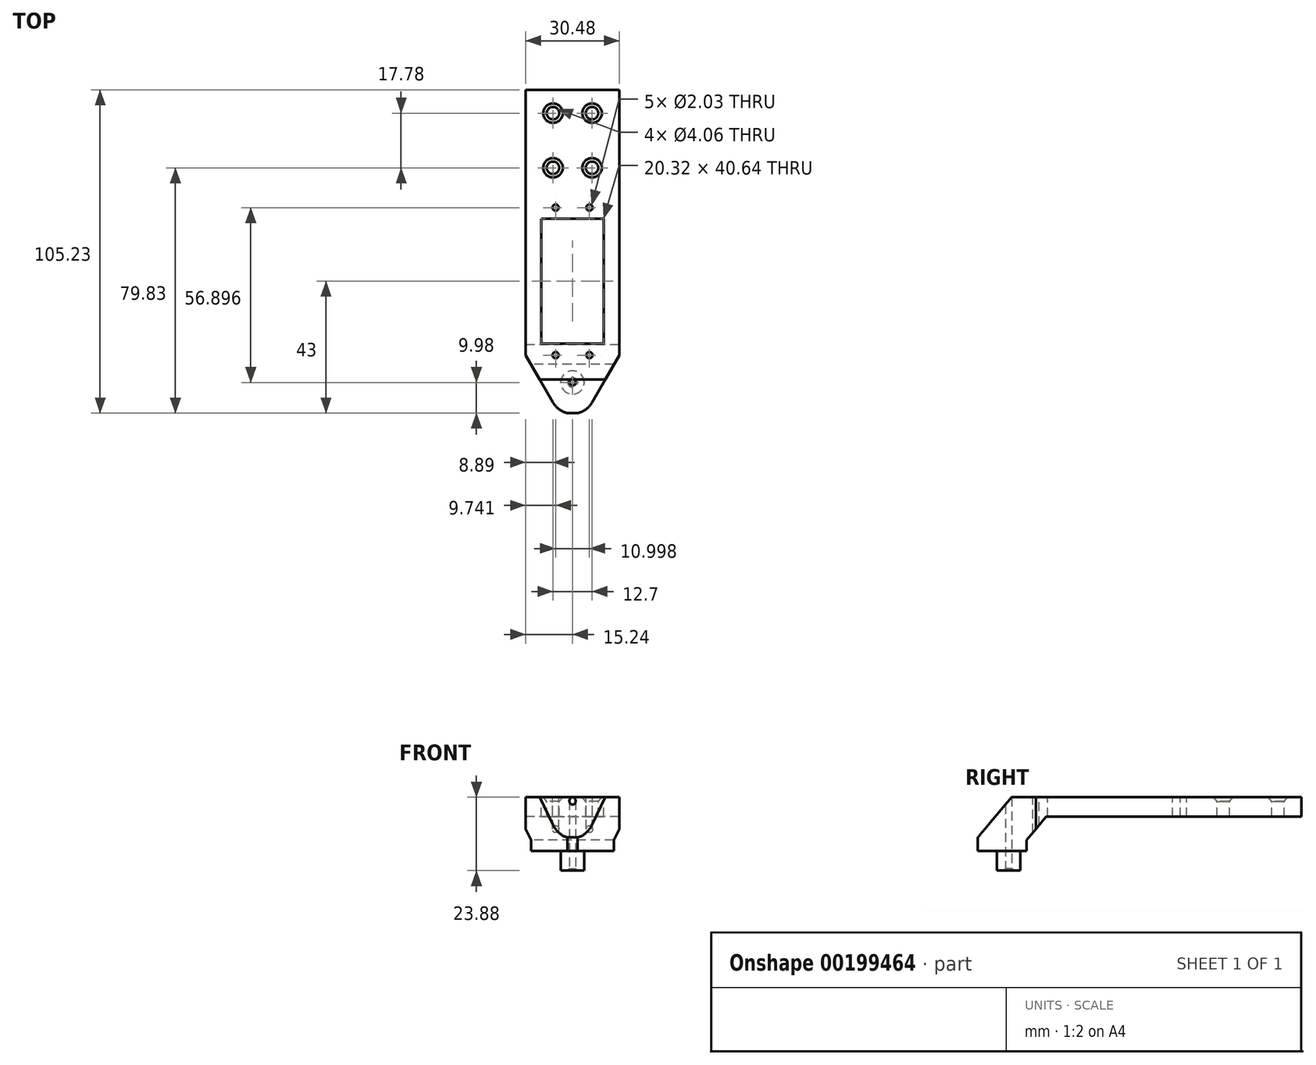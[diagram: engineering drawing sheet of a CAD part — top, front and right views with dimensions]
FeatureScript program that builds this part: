
annotation { "Feature Type Name" : "Feature", "Feature Type Description" : "" }
export const myFeature = defineFeature(function(context is Context, id is Id, definition is map)
    precondition{}
    {
        {
            var Q0;
            Q0=qCreatedBy(makeId("Top.planeOp"),FACE);
            var sketch = newSketch(context, id + "F0", { "sketchPlane" : qUnion([Q0])});
            skCircle(sketch, "E0", {"center": v(0, 0) * mm, "radius": 6.35 * mm});
            skLineSegment(sketch, "E1", {"start": v(-10.16, -10.16) * mm, "end": v(10.16, -10.16) * mm});
            skLineSegment(sketch, "E2", {"start": v(10.16, -10.16) * mm, "end": v(10.16, 30.48) * mm});
            skLineSegment(sketch, "E3", {"start": v(10.16, 30.48) * mm, "end": v(-10.16, 30.48) * mm});
            skLineSegment(sketch, "E4", {"start": v(-10.16, 30.48) * mm, "end": v(-10.16, -10.16) * mm});
            skLineSegment(sketch, "E5", {"start": v(15.24, -13.97) * mm, "end": v(-15.24, -13.97) * mm});
            skLineSegment(sketch, "E6", {"start": v(-15.24, -13.97) * mm, "end": v(-15.24, 40.64) * mm});
            skLineSegment(sketch, "E7", {"start": v(-15.24, 40.64) * mm, "end": v(15.24, 40.64) * mm});
            skLineSegment(sketch, "E8", {"start": v(15.24, 40.64) * mm, "end": v(15.24, -13.97) * mm});
            skPoint(sketch, "E9", {"position": v(-5.5, 34.04) * mm});
            skPoint(sketch, "E10", {"position": v(5.5, 34.04) * mm});
            skCircle(sketch, "E11", {"center": v(0, -22.86) * mm, "radius": 3.81 * mm, "construction": true});
            skCircle(sketch, "E12", {"center": v(-5.5, 34.04) * mm, "radius": 1.02 * mm});
            skCircle(sketch, "E13", {"center": v(5.5, 34.04) * mm, "radius": 1.02 * mm});
            skCircle(sketch, "E14", {"center": v(-5.5, -13.97) * mm, "radius": 1.02 * mm});
            skCircle(sketch, "E15", {"center": v(5.5, -13.97) * mm, "radius": 1.02 * mm});
            skLineSegment(sketch, "E16", {"start": v(15.24, -13.97) * mm, "end": v(6.35, -29.37) * mm});
            skLineSegment(sketch, "E17", {"start": v(-15.24, -13.97) * mm, "end": v(-6.35, -29.37) * mm});
            skArc(sketch, "E18", {"start": v(-6.35, -29.37) * mm, "mid": v(0, -33.03) * mm, "end": v(6.35, -29.37) * mm});
            skLineSegment(sketch, "E19", {"start": v(-15.24, 40.64) * mm, "end": v(-15.24, 72.4) * mm});
            skLineSegment(sketch, "E20", {"start": v(-15.24, 72.4) * mm, "end": v(15.24, 72.4) * mm});
            skLineSegment(sketch, "E21", {"start": v(15.24, 72.4) * mm, "end": v(15.24, 40.64) * mm});
            skPoint(sketch, "E22", {"position": v(0, 72.4) * mm});
            skLineSegment(sketch, "E23", {"start": v(0, 72.4) * mm, "end": v(0, 40.64) * mm});
            skPoint(sketch, "E24", {"position": v(6.35, 64.77) * mm});
            skPoint(sketch, "E25", {"position": v(6.35, 47) * mm});
            skPoint(sketch, "E26", {"position": v(-6.35, 64.77) * mm});
            skPoint(sketch, "E27", {"position": v(-6.35, 47) * mm});
            skSolve(sketch);
        }
        {
            var Q0;
            Q0=qCreatedBy(makeId("Right.planeOp"),FACE);
            var sketch = newSketch(context, id + "F1", { "sketchPlane" : qUnion([Q0])});
            skPoint(sketch, "E28", {"position": v(-21.85, 0) * mm});
            skPoint(sketch, "E29", {"position": v(40.64, 0) * mm});
            skLineSegment(sketch, "E30", {"start": v(40.64, 0) * mm, "end": v(-21.85, 0) * mm});
            skLineSegment(sketch, "E31", {"start": v(40.64, 0) * mm, "end": v(40.64, -6.35) * mm});
            skPoint(sketch, "E32", {"position": v(-10.16, 0) * mm});
            skPoint(sketch, "E33", {"position": v(-10.6, -6.35) * mm});
            skLineSegment(sketch, "E34", {"start": v(40.64, -6.35) * mm, "end": v(-10.6, -6.35) * mm});
            skLineSegment(sketch, "E35", {"start": v(-10.6, -6.35) * mm, "end": v(-16.99, -13.97) * mm});
            skLineSegment(sketch, "E36", {"start": v(-16.99, -17.53) * mm, "end": v(-32.84, -17.53) * mm});
            skLineSegment(sketch, "E37", {"start": v(-16.99, -13.97) * mm, "end": v(-16.99, -17.53) * mm});
            skLineSegment(sketch, "E38", {"start": v(-32.84, -17.53) * mm, "end": v(-32.84, -13.97) * mm});
            skLineSegment(sketch, "E39", {"start": v(-32.84, -13.97) * mm, "end": v(-32.84, -13.1) * mm});
            skLineSegment(sketch, "E40", {"start": v(-32.84, -13.1) * mm, "end": v(-21.85, 0) * mm});
            skLineSegment(sketch, "E41", {"start": v(40.64, 0) * mm, "end": v(83.81, 0) * mm});
            skLineSegment(sketch, "E42", {"start": v(83.81, 0) * mm, "end": v(83.81, -6.35) * mm});
            skLineSegment(sketch, "E43", {"start": v(83.81, -6.35) * mm, "end": v(40.64, -6.35) * mm});
            skSolve(sketch);
        }
        {
            var Q0;
            Q0 = qSketchRegion(id + "F0", true);
            var Q1;
            Q1=sQuery(id+"F1.wireOp",VERTEX,"E38.start");
            extrude(context, id + "F2", {"entities" : qUnion([Q0]), "endBound" : BoundingType.UP_TO_VERTEX, "oppositeDirection" : true, "endBoundEntityVertex" : qUnion([Q1]), "depth" : 25.4 * mm});
        }
        {
            var Q0;
            Q0 = qSketchRegion(id + "F1", true);
            extrude(context, id + "F3", {"entities" : qUnion([Q0]), "operationType" : NewBodyOperationType.INTERSECT, "endBound" : BoundingType.SYMMETRIC, "depth" : 254 * mm});
        }
        {
            var Q0;
            Q0=makeQuery(id+"F2.opExtrude","CAP_FACE",FACE,{"disambiguationData":[OSD([sQuery(id+"F0.wireOp",EDGE,"E1"),sQuery(id+"F0.wireOp",EDGE,"E2"),sQuery(id+"F0.wireOp",EDGE,"E3"),sQuery(id+"F0.wireOp",EDGE,"E4"),sQuery(id+"F0.wireOp",EDGE,"E6"),sQuery(id+"F0.wireOp",EDGE,"E8"),sQuery(id+"F0.wireOp",EDGE,"E12"),sQuery(id+"F0.wireOp",EDGE,"E13"),sQuery(id+"F0.wireOp",EDGE,"E14"),sQuery(id+"F0.wireOp",EDGE,"E15"),sQuery(id+"F0.wireOp",EDGE,"E16"),sQuery(id+"F0.wireOp",EDGE,"E17"),sQuery(id+"F0.wireOp",EDGE,"E18"),sQuery(id+"F0.wireOp",EDGE,"E19"),sQuery(id+"F0.wireOp",EDGE,"E20"),sQuery(id+"F0.wireOp",EDGE,"E21")])],"isStart":false});
            var sketch = newSketch(context, id + "F4", { "sketchPlane" : qUnion([Q0])});
            skPoint(sketch, "E44", {"position": v(0, 22.86) * mm});
            skCircle(sketch, "E45", {"center": v(0, 22.86) * mm, "radius": 3.81 * mm});
            skSolve(sketch);
        }
        {
            var Q0;
            Q0 = qSketchRegion(id + "F4", true);
            extrude(context, id + "F5", {"entities" : qUnion([Q0]), "operationType" : NewBodyOperationType.ADD, "depth" : 6.35 * mm});
        }
        {
            var Q0;
            Q0=makeQuery(id+"F5.opExtrude","CAP_FACE",FACE,{"disambiguationData":[OSD([sQuery(id+"F4.wireOp",EDGE,"E45")])],"isStart":false});
            var sketch = newSketch(context, id + "F6", { "sketchPlane" : qUnion([Q0])});
            skPoint(sketch, "E46", {"position": v(0, 22.86) * mm});
            skSolve(sketch);
        }
        {
            var Q0;
            Q0=sQuery(id+"F6.wireOp",VERTEX,"E46");
            var Q1;
            Q1=makeQuery(id+"F2.opExtrude","SWEPT_BODY",BODY,{"disambiguationData":[OSD([sQuery(id+"F0.wireOp",EDGE,"E1"),sQuery(id+"F0.wireOp",EDGE,"E2"),sQuery(id+"F0.wireOp",EDGE,"E3"),sQuery(id+"F0.wireOp",EDGE,"E4"),sQuery(id+"F0.wireOp",EDGE,"E6"),sQuery(id+"F0.wireOp",EDGE,"E8"),sQuery(id+"F0.wireOp",EDGE,"E12"),sQuery(id+"F0.wireOp",EDGE,"E13"),sQuery(id+"F0.wireOp",EDGE,"E14"),sQuery(id+"F0.wireOp",EDGE,"E15"),sQuery(id+"F0.wireOp",EDGE,"E16"),sQuery(id+"F0.wireOp",EDGE,"E17"),sQuery(id+"F0.wireOp",EDGE,"E18"),sQuery(id+"F0.wireOp",EDGE,"E19"),sQuery(id+"F0.wireOp",EDGE,"E20"),sQuery(id+"F0.wireOp",EDGE,"E21")])]});
            hole(context, id + "F7", {"style" : HoleStyle.C_SINK, "endStyle" : HoleEndStyle.THROUGH, "holeDiameter" : 2.03 * mm, "cSinkDiameter" : 3.17 * mm, "cSinkAngle" : 82 * degree, "locations" : qUnion([Q0]), "scope" : qUnion([Q1]), "isTappedThrough" : true});
        }
        {
            var Q0;
            Q0=sQuery(id+"F0.wireOp",VERTEX,"E25");
            var Q1;
            Q1=sQuery(id+"F0.wireOp",VERTEX,"E27");
            var Q2;
            Q2=sQuery(id+"F0.wireOp",VERTEX,"E26");
            var Q3;
            Q3=sQuery(id+"F0.wireOp",VERTEX,"E24");
            var Q4;
            Q4=makeQuery(id+"F2.opExtrude","SWEPT_BODY",BODY,{"disambiguationData":[OSD([sQuery(id+"F0.wireOp",EDGE,"E1"),sQuery(id+"F0.wireOp",EDGE,"E2"),sQuery(id+"F0.wireOp",EDGE,"E3"),sQuery(id+"F0.wireOp",EDGE,"E4"),sQuery(id+"F0.wireOp",EDGE,"E6"),sQuery(id+"F0.wireOp",EDGE,"E8"),sQuery(id+"F0.wireOp",EDGE,"E12"),sQuery(id+"F0.wireOp",EDGE,"E13"),sQuery(id+"F0.wireOp",EDGE,"E14"),sQuery(id+"F0.wireOp",EDGE,"E15"),sQuery(id+"F0.wireOp",EDGE,"E16"),sQuery(id+"F0.wireOp",EDGE,"E17"),sQuery(id+"F0.wireOp",EDGE,"E18"),sQuery(id+"F0.wireOp",EDGE,"E19"),sQuery(id+"F0.wireOp",EDGE,"E20"),sQuery(id+"F0.wireOp",EDGE,"E21")])]});
            hole(context, id + "F8", {"style" : HoleStyle.C_SINK, "endStyle" : HoleEndStyle.THROUGH, "holeDiameter" : 4.06 * mm, "cSinkDiameter" : 6.35 * mm, "cSinkAngle" : 82 * degree, "startFromSketch" : true, "locations" : qUnion([Q0, Q1, Q2, Q3]), "scope" : qUnion([Q4]), "isTappedThrough" : true});
        }
    });
